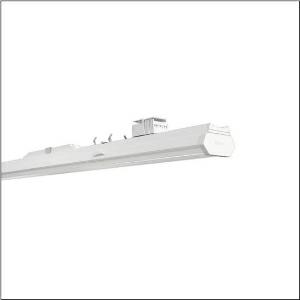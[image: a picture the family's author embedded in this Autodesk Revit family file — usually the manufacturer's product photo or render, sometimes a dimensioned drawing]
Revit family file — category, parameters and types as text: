
# Revit family: licross_r__11_protected_mo_51ts12vn465f_67ab
name_source: partatom
category: Lighting Fixtures
units: mm (PartAtom-declared; Revit-internal decimal feet)

## family parameters
Cut with Voids When Loaded = No
Host = Face
Light Source = No
Part Type = Normal
Room Calculation Point = No
Round Connector Dimension = Use Diameter
Shared = No

## types (1)
- --- (1 x LED, 6530 lm, 42.6 W, 4000K)
    Apparent Load = 43 VA
    CIE Flux Codes = 54 82 95 97 100
    Color Rendering = 80
    Color Temperature = 4000K
    Default Elevation = 1800 mm
    Description = Licross® 11 Protected MOluminaire insert, length: 1.500mm, width: 90mm, height: 101mm, LED rated luminous flux: 6.530lm, light colour: 840, control gear: DALI 2, CLO, control gear: ECG DALI, with plug, 5-pole, with phase selection, mains connection: 220..240V, AC, 50/60Hz, halogen-free wiring, primary optical cover: cover, of PMMA, light emission: direct with ceiling illumination distribution, protection rating (complete): IP50, insulation class (complete): insulation class I (protective earthing), certification: CE, ENEC, VDE, UKCA, protection symbol: D if used in an environment with non-conductive dust loads with corresponding accessories, permissible ambient temperature for indoor applications: -25..+40°C, corresponds to IFS (International Featured Standards) requirements for safety and quality in the food industry, reducing of maximum allowable ambient temperature of 5°C with ceiling mounting, packaging unit: 1 piece
    Height = 92 mm
    Lamp = 1 x LED
    Lamp Light Flux = 6530 lm
    Lamp Power = 42.6 W
    Lamp count = 1
    Length = 1500 mm
    Luminous efficacy = 153 lm/W
    Manufacturer = Siteco
    ModVariant = No
    Model = 51TS12VN465F
    Mounting Place = Ceiling
    Mounting Type = Pendant
    Number of Poles = 1
    OnlyDefault = Yes
    Power Factor = 1
    Product Name = Licross® 11 Protected MO
    Product group = luminaire insert
    ProductGroupID = 902
    Protection Class = Protection class I
    Protection Degree = IP 50
    RLX_Detail_Level = 1
    RlxData = <blob elided: 24145 chars, md5=9591eac5>
    Socket = socket
    Standby Power = 0 W
    System Light Flux = 6530 lm
    System Power = 43 W
    Type Comments = factory setting: luminous flux: 100 % | dim-lin: 254 | 280 mA
    Type Image = l_1256145.jpg
    URL = http://relux.com
    VarID = @adj_129449
    Voltage = 0 V
    Weight = 0.00 kg
    Width = 88 mm

## geometry (parser evidence)
native form markers: Blend x4, Sweep x11
no freeform markers — native parametric forms only
